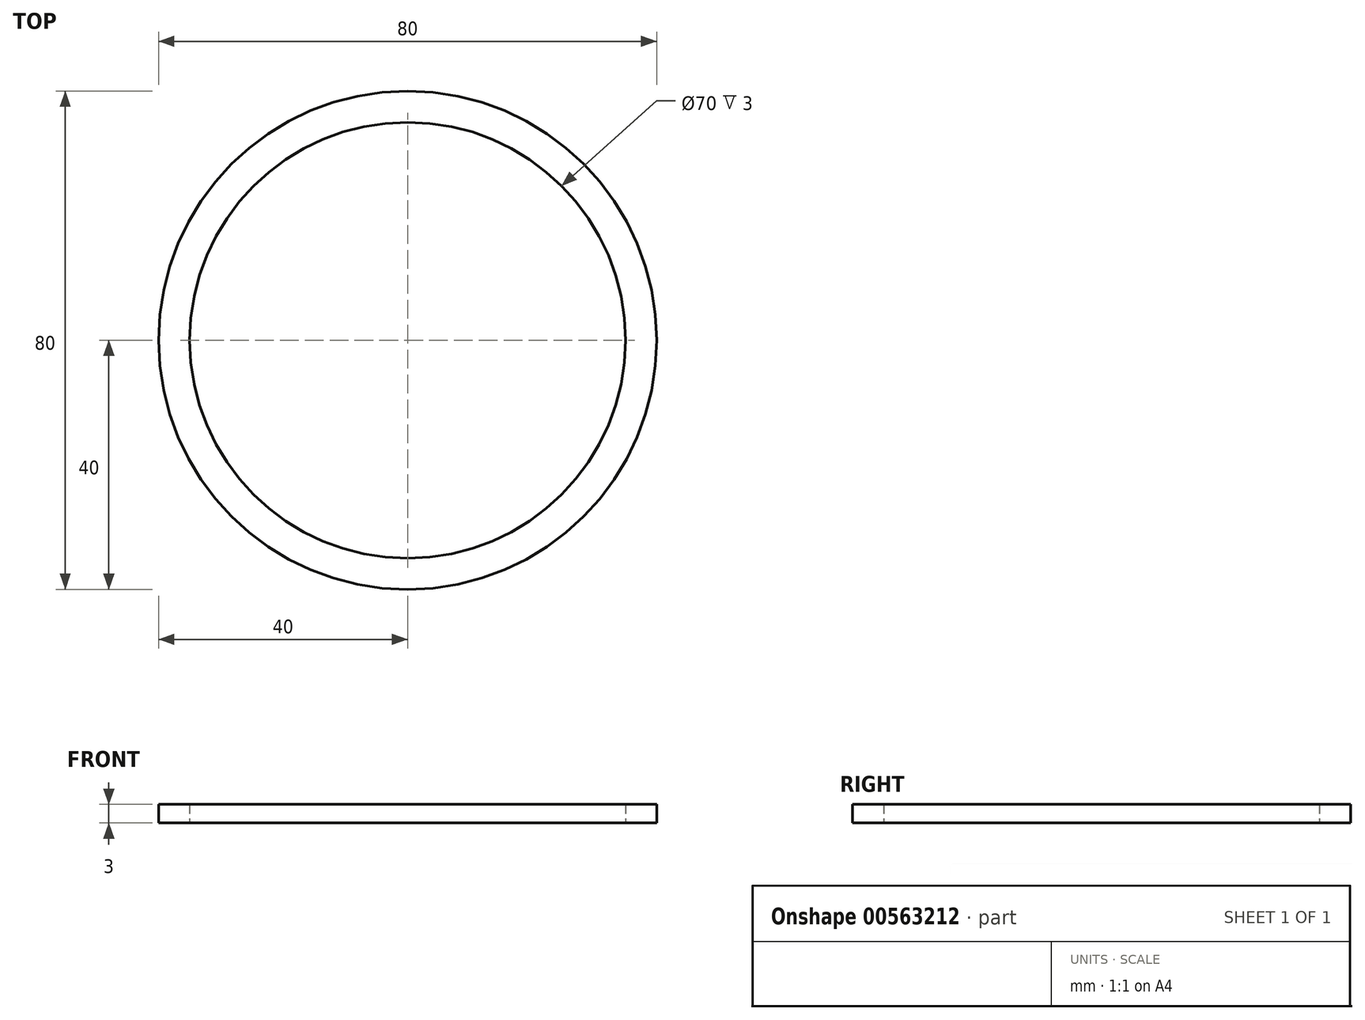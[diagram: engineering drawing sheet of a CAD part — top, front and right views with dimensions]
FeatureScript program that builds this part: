
annotation { "Feature Type Name" : "Feature", "Feature Type Description" : "" }
export const myFeature = defineFeature(function(context is Context, id is Id, definition is map)
    precondition{}
    {
        {
            var Q0;
            Q0=qCreatedBy(makeId("Top.planeOp"),FACE);
            var sketch = newSketch(context, id + "F0", { "sketchPlane" : qUnion([Q0])});
            skCircle(sketch, "E0", {"center": v(0, 0) * mm, "radius": 40 * mm});
            skCircle(sketch, "E1", {"center": v(0, 0) * mm, "radius": 35 * mm});
            skSolve(sketch);
        }
        {
            var Q0;
            Q0=qSketchRegion(id+"F0",true);
            extrude(context, id + "F1", {"entities" : qUnion([Q0]), "endBound" : BoundingType.SYMMETRIC, "depth" : 3 * mm, "offsetDistance" : 25 * mm});
        }
    });
